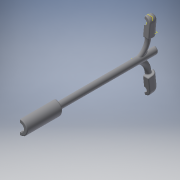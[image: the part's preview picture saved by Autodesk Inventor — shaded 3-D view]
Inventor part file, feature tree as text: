
AUTODESK INVENTOR PART (.ipt)
format: ipt  version: 2018 (Build 220112000, 112)  size: 449,024 bytes
history: native  units: mm
features: sketch x10, extrude x9, fillet x6, projected_geometry x4, plane x3, revolve x1, sweep x1, mirror x1
ambient origin geometry x8: Origin, YZ Plane, XZ Plane, XY Plane, X Axis, Y Axis, Z Axis, Center Point
bodies: Solid1 (feature_tree)
feature tree (35):
  revolve  "Revolution1"  [1 undecoded]
  fillet  "Fillet1"  Radius=8.0mm
  fillet  "Fillet2"  Radius=40.0mm
  fillet  "Fillet3"  [1 undecoded]
  plane  "Work Plane1"
  sweep  "Sweep1"
  extrude  "Extrusion2"  Depth=1.0mm
  fillet  "Fillet4"  Radius=1.5mm
  fillet  "Fillet5"  Radius=1.0mm
  extrude  "Extrusion3"  Depth=4.0mm
  extrude  "Extrusion4"  Depth=2.0mm
  extrude  "Extrusion5"  Depth=1.0mm
  extrude  "Extrusion6"  Depth=18.0mm
  extrude  "Extrusion7"  Depth=16.0mm
  plane  "Work Plane3"
  extrude  "Extrusion8"  Depth=12.0mm
  extrude  "Extrusion9"  Depth=0.5mm
  plane  "Work Plane4"
  extrude  "Extrusion10"  Depth=0.5mm
  fillet  "Fillet6"  Radius=20.0mm
  mirror  "Mirror2"
  sketch  "Sketch6"  dims[d0=150.0mm d1=4.0mm d3=8.0mm d4=40.0mm d5=90.0deg]
  sketch  "Sketch8"  dims[d20=1.5mm d21=1.5mm]
  projected_geometry  "Projected Loop3"
  sketch  "Sketch10"  dims[d22=1.5mm d23=1.0mm d24=1.5mm d25=1.0mm]
  projected_geometry  "Projected Loop4"
  sketch  "Sketch11"  dims[d26=1.5mm d27=4.0mm]
  sketch  "Sketch12"  dims[d29=9.0mm d30=2.0mm]
  sketch  "Sketch13"  dims[d31=1.0mm d32=1.0mm]
  sketch  "Sketch14"  dims[d33=-23.0mm d38=18.0mm]
  sketch  "Sketch15"  dims[d39=18.0mm d40=16.0mm]
  projected_geometry  "Projected Loop5"
  sketch  "Sketch16"  dims[d41=0.0mm d42=0.0mm d43=12.0mm]
  sketch  "Sketch17"  dims[d44=5.0mm d45=6.0mm d46=6.0mm d47=20.0mm d48=0.0mm d49=6.0mm d50=1.0mm d51=5.0mm d52=6.0mm d53=8.0mm d54=0.0mm d55=10.0mm d56=0.0mm d57=50.0mm d58=0.0mm d59=2.0mm d60=0.0mm d61=8.0mm d62=15.0mm d63=0.0mm d64=-3.0mm d65=7.0mm d66=1.1mm d67=0.0mm d68=10.0mm d69=0.0mm d70=-3.0mm d71=10.0mm d72=0.0mm d73=0.5mm d74=8.25mm]
  projected_geometry  "Projected Loop6"
note: 2 required parameter values undecoded (feature->parameter linkage not recoverable at this tier; creation-order binding heuristic only, values carry confidence <= 0.55)